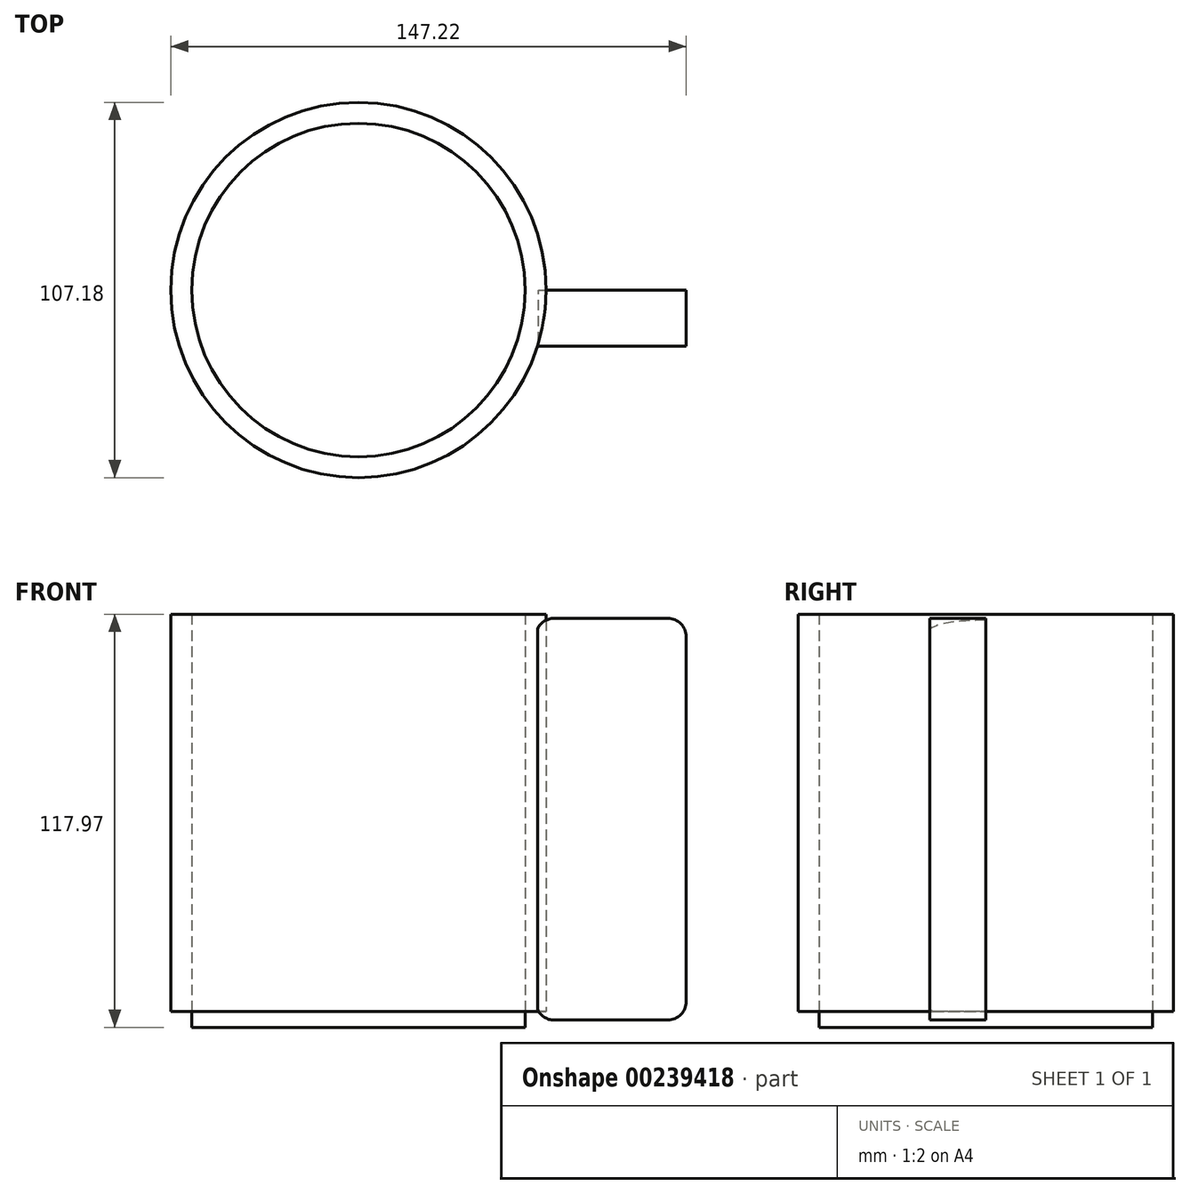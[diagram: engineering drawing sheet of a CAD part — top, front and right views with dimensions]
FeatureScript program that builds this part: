
annotation { "Feature Type Name" : "Feature", "Feature Type Description" : "" }
export const myFeature = defineFeature(function(context is Context, id is Id, definition is map)
    precondition{}
    {
        {
            var Q0;
            Q0=qCreatedBy(makeId("Top.planeOp"),FACE);
            var sketch = newSketch(context, id + "F0", { "sketchPlane" : qUnion([Q0])});
            skCircle(sketch, "E0", {"center": v(0, 0) * mm, "radius": 47.63 * mm});
            skCircle(sketch, "E1", {"center": v(0, 0) * mm, "radius": 53.59 * mm});
            skSolve(sketch);
        }
        {
            var Q0;
            Q0=makeQuery(id+"F0.imprint","IMPRINT",FACE,{"disambiguationData":[TD([[makeQuery(id+"F0.imprint","IMPRINT",EDGE,{"derivedFrom":sQuery(id+"F0.wireOp",EDGE,"E0")}),-1.0]])]});
            extrude(context, id + "F1", {"entities" : qUnion([Q0]), "depth" : 113.4 * mm});
        }
        {
            var Q0;
            Q0=makeQuery(id+"F0.imprint","IMPRINT",FACE,{"disambiguationData":[TD([[makeQuery(id+"F0.imprint","IMPRINT",EDGE,{"derivedFrom":sQuery(id+"F0.wireOp",EDGE,"E0")}),1.0]])]});
            extrude(context, id + "F2", {"entities" : qUnion([Q0]), "oppositeDirection" : true, "depth" : 4.57 * mm});
        }
        {
            var Q0;
            Q0=qCreatedBy(makeId("Front.planeOp"),FACE);
            var sketch = newSketch(context, id + "F3", { "sketchPlane" : qUnion([Q0])});
            skLineSegment(sketch, "E2.bottom", {"start": v(55.9, 112.23) * mm, "end": v(88.39, 112.23) * mm});
            skLineSegment(sketch, "E2.top", {"start": v(55.9, -2.5) * mm, "end": v(88.39, -2.5) * mm});
            skLineSegment(sketch, "E2.left", {"start": v(50.67, 106.99) * mm, "end": v(50.67, 2.75) * mm});
            skLineSegment(sketch, "E2.right", {"start": v(93.63, 106.99) * mm, "end": v(93.63, 2.75) * mm});
            skPoint(sketch, "E3.visualSharp", {"position": v(93.63, -2.5) * mm});
            skArc(sketch, "E3.filletArc", {"start": v(88.39, -2.5) * mm, "mid": v(92.1, -0.96) * mm, "end": v(93.63, 2.75) * mm});
            skPoint(sketch, "E4.visualSharp", {"position": v(93.63, 112.23) * mm});
            skArc(sketch, "E4.filletArc", {"start": v(93.63, 106.99) * mm, "mid": v(92.1, 110.7) * mm, "end": v(88.39, 112.23) * mm});
            skPoint(sketch, "E5.visualSharp", {"position": v(50.67, 112.23) * mm});
            skArc(sketch, "E5.filletArc", {"start": v(55.9, 112.23) * mm, "mid": v(52.2, 110.7) * mm, "end": v(50.67, 106.99) * mm});
            skPoint(sketch, "E6.visualSharp", {"position": v(50.67, -2.5) * mm});
            skArc(sketch, "E6.filletArc", {"start": v(50.67, 2.75) * mm, "mid": v(52.2, -0.96) * mm, "end": v(55.9, -2.5) * mm});
            skSolve(sketch);
        }
        {
            var Q0;
            Q0=makeQuery(id+"F3.imprint","IMPRINT",FACE,{"disambiguationData":[TD([[makeQuery(id+"F3.imprint","IMPRINT",EDGE,{"derivedFrom":sQuery(id+"F3.wireOp",EDGE,"E2.bottom")}),-1.0]])]});
            extrude(context, id + "F4", {"entities" : qUnion([Q0]), "operationType" : NewBodyOperationType.ADD, "depth" : 16 * mm});
        }
    });
